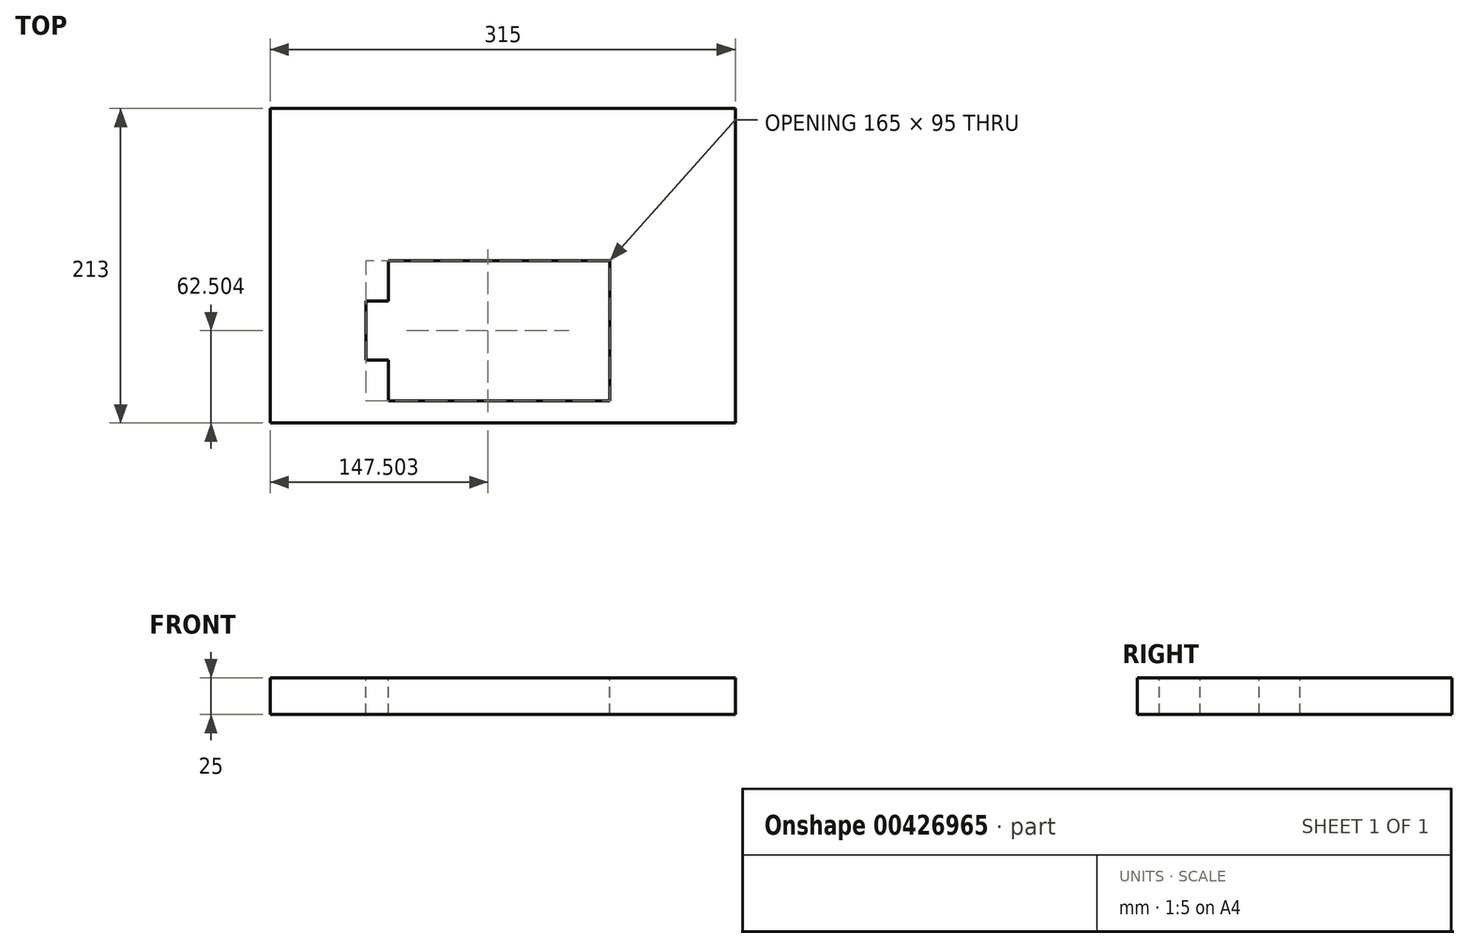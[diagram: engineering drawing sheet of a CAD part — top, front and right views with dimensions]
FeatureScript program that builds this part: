
annotation { "Feature Type Name" : "Feature", "Feature Type Description" : "" }
export const myFeature = defineFeature(function(context is Context, id is Id, definition is map)
    precondition{}
    {
        {
            var Q0;
            Q0=qCreatedBy(makeId("Top.planeOp"),FACE);
            var sketch = newSketch(context, id + "F0", { "sketchPlane" : qUnion([Q0])});
            skLineSegment(sketch, "E0.bottom", {"start": v(-153.95, 134.37) * mm, "end": v(161.05, 134.37) * mm});
            skLineSegment(sketch, "E0.top", {"start": v(-153.95, -78.63) * mm, "end": v(161.05, -78.63) * mm});
            skLineSegment(sketch, "E0.left", {"start": v(-153.95, 134.37) * mm, "end": v(-153.95, -78.63) * mm});
            skLineSegment(sketch, "E0.right", {"start": v(161.05, 134.37) * mm, "end": v(161.05, -78.63) * mm});
            skSolve(sketch);
        }
        {
            var Q0;
            Q0 = qSketchRegion(id + "F0", true);
            extrude(context, id + "F1", {"entities" : qUnion([Q0]), "depth" : 25 * mm, "offsetDistance" : 25 * mm});
        }
        {
            var Q0;
            Q0=makeQuery(id+"F1.opExtrude","CAP_FACE",FACE,{"disambiguationData":[OSD([sQuery(id+"F0.wireOp",EDGE,"E0.bottom"),sQuery(id+"F0.wireOp",EDGE,"E0.top"),sQuery(id+"F0.wireOp",EDGE,"E0.left"),sQuery(id+"F0.wireOp",EDGE,"E0.right")])],"isStart":false});
            var sketch = newSketch(context, id + "F2", { "sketchPlane" : qUnion([Q0])});
            skLineSegment(sketch, "E1.bottom", {"start": v(-73.95, 31.37) * mm, "end": v(76.05, 31.37) * mm});
            skLineSegment(sketch, "E1.top", {"start": v(-73.95, -63.63) * mm, "end": v(76.05, -63.63) * mm});
            skLineSegment(sketch, "E1.left", {"start": v(-73.95, 31.37) * mm, "end": v(-73.95, -63.63) * mm});
            skLineSegment(sketch, "E1.right", {"start": v(76.05, 31.37) * mm, "end": v(76.05, -63.63) * mm});
            skLineSegment(sketch, "E2.bottom", {"start": v(-73.95, 3.87) * mm, "end": v(-88.95, 3.87) * mm});
            skLineSegment(sketch, "E2.top", {"start": v(-73.95, -36.13) * mm, "end": v(-88.95, -36.13) * mm});
            skLineSegment(sketch, "E2.left", {"start": v(-73.95, 3.87) * mm, "end": v(-73.95, -36.13) * mm});
            skLineSegment(sketch, "E2.right", {"start": v(-88.95, 3.87) * mm, "end": v(-88.95, -36.13) * mm});
            skSolve(sketch);
        }
        {
            var Q0;
            {var subQ3=sQuery(id+"F2.wireOp",EDGE,"E1.bottom");Q0=makeQuery(id+"F2.imprint","IMPRINT",FACE,{"disambiguationData":[TD([[makeQuery(id+"F2.imprint","IMPRINT",EDGE,{"derivedFrom":subQ3}),-1.0]])]});}
            var Q1;
            Q1=makeQuery(id+"F2.imprint","IMPRINT",FACE,{"disambiguationData":[TD([[makeQuery(id+"F2.imprint","IMPRINT",EDGE,{"derivedFrom":sQuery(id+"F2.wireOp",EDGE,"E2.bottom")}),1.0]])]});
            extrude(context, id + "F3", {"entities" : qUnion([Q0, Q1]), "operationType" : NewBodyOperationType.REMOVE, "oppositeDirection" : true, "depth" : 25 * mm, "offsetDistance" : 25 * mm});
        }
    });
